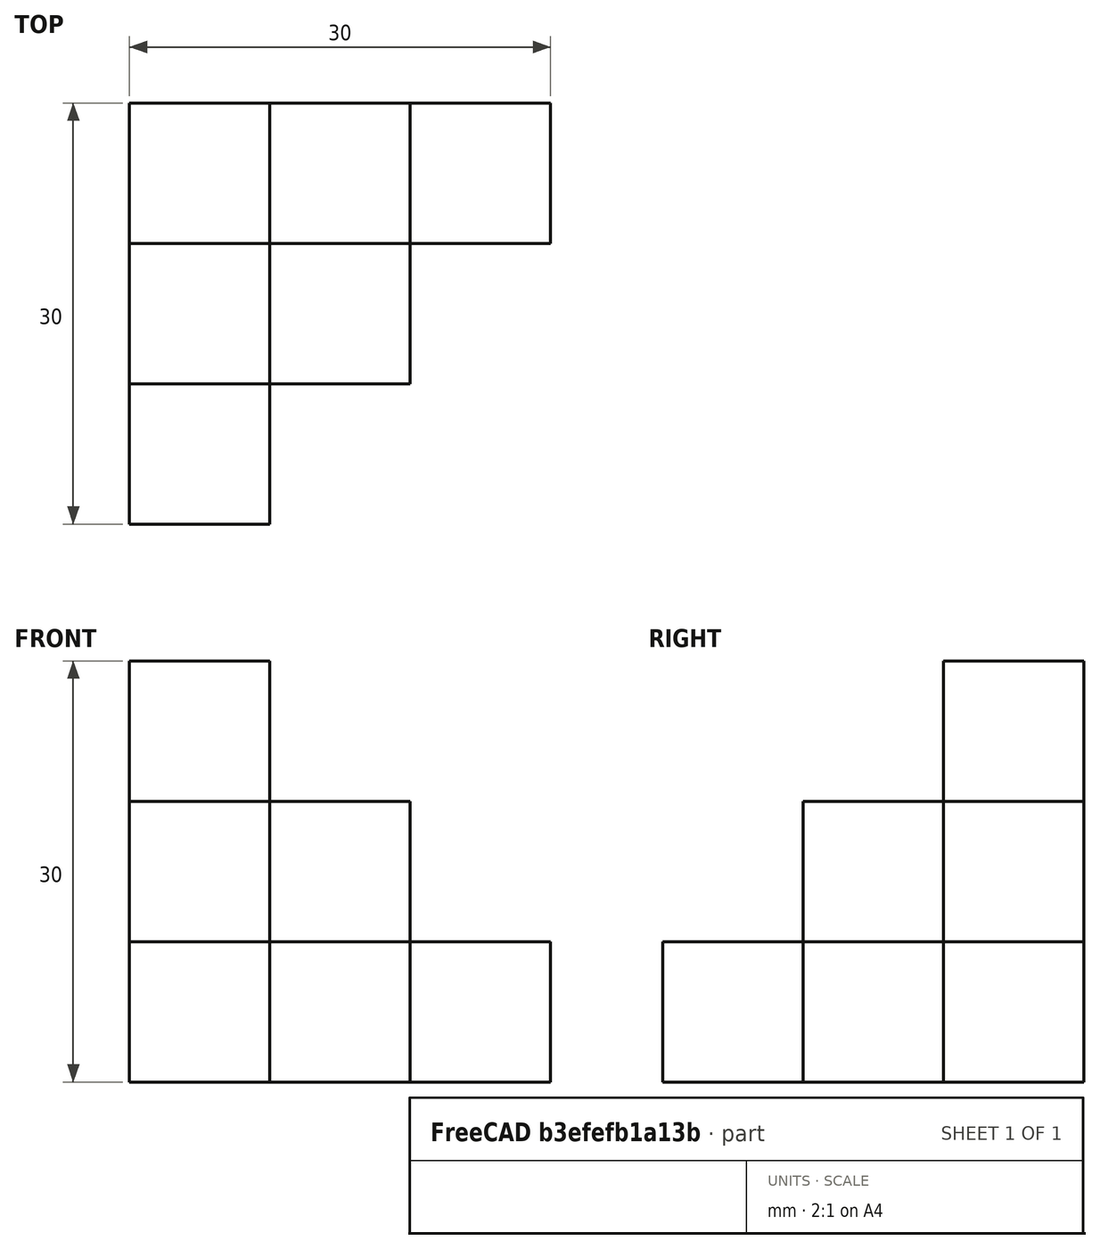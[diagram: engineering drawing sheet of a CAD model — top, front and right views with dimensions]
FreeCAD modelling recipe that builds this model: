
FCSTD DOCUMENT  (FreeCAD 0.21R33694 (Git))
Label: OJT1_T04R01_qubert3
License: All rights reserved
LicenseURL: http://en.wikipedia.org/wiki/All_rights_reserved
objects: Part::Box×6
note: 6 computed .brp shape members not serialized (recipe doc carries the construction recipe); baked Part::Feature solids carry a one-line shape summary decoded from their .brp

FEATURE [Part::Box] Box  label="Cube"
  AttacherType = Attacher::AttachEngine3D
  Height = 20
  Length = 10
  Width = 10
FEATURE [Part::Box] Box001  label="Cube001"
  AttacherType = Attacher::AttachEngine3D
  Height = 30
  Length = 10
  Placement = pos=(-10,0,0) rot=(0,0,1;0rad)
  Width = 10
FEATURE [Part::Box] Box002  label="Cube002"
  AttacherType = Attacher::AttachEngine3D
  Height = 20
  Length = 10
  Placement = pos=(-10,-10,0) rot=(0,0,1;0rad)
  Width = 10
FEATURE [Part::Box] Box003  label="Cube003"
  AttacherType = Attacher::AttachEngine3D
  Height = 10
  Length = 10
  Placement = pos=(10,0,0) rot=(0,0,1;0rad)
  Width = 10
FEATURE [Part::Box] Box004  label="Cube004"
  AttacherType = Attacher::AttachEngine3D
  Height = 10
  Length = 10
  Placement = pos=(-10,-20,0) rot=(0,0,1;0rad)
  Width = 10
FEATURE [Part::Box] Box005  label="Cube005"
  AttacherType = Attacher::AttachEngine3D
  Height = 10
  Length = 10
  Placement = pos=(0,-10,0) rot=(0,0,1;0rad)
  Width = 10
